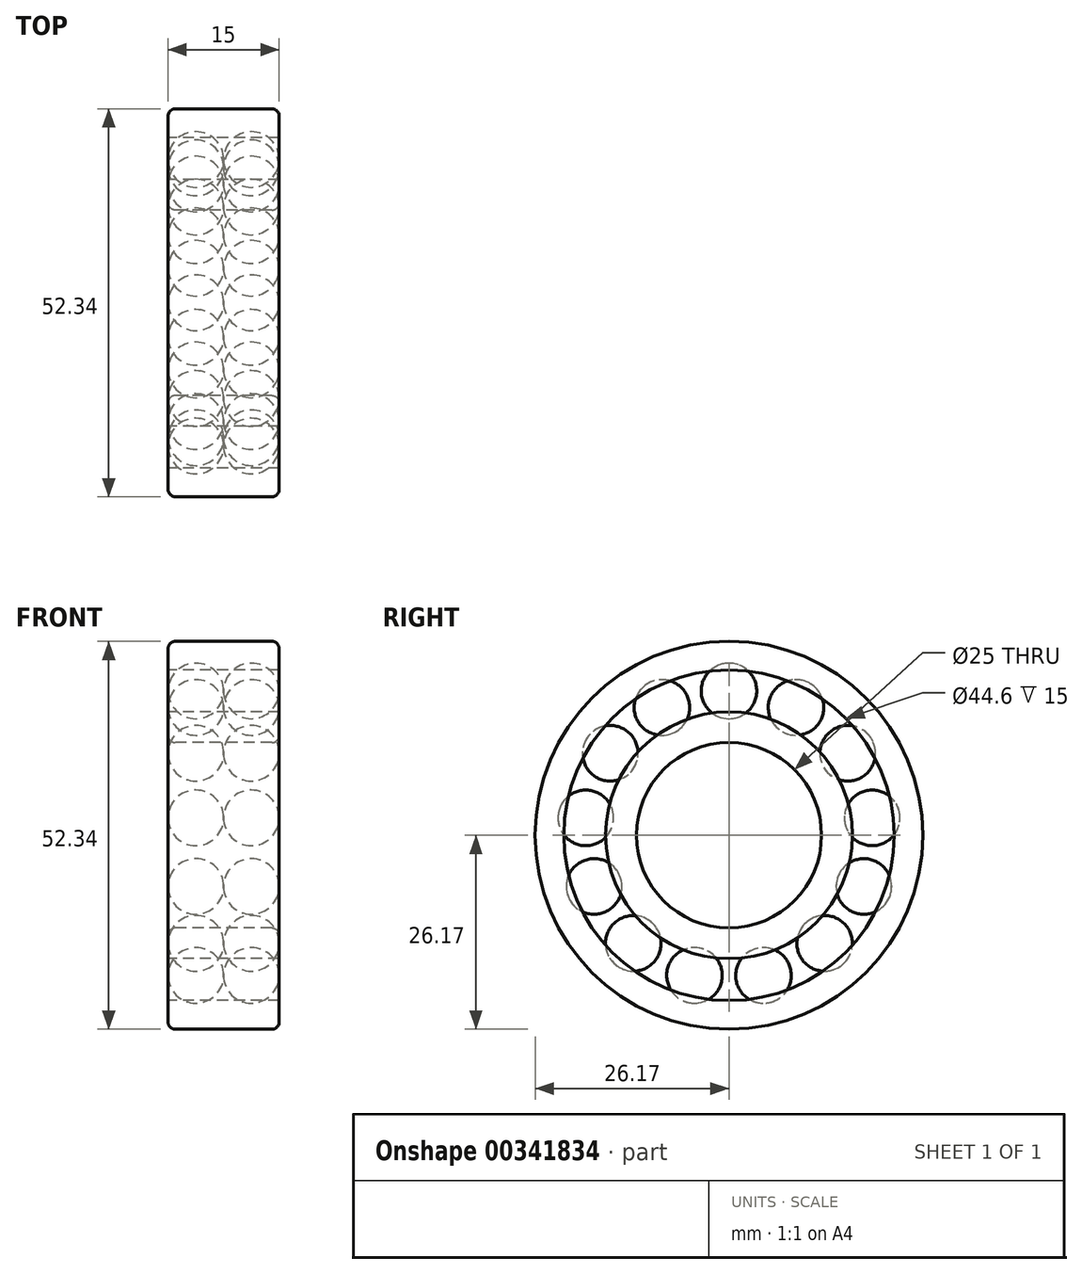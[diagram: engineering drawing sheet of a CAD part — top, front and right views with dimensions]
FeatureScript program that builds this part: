
annotation { "Feature Type Name" : "Feature", "Feature Type Description" : "" }
export const myFeature = defineFeature(function(context is Context, id is Id, definition is map)
    precondition{}
    {
        {
            var Q0;
            Q0=qCreatedBy(makeId("Front.planeOp"),FACE);
            var sketch = newSketch(context, id + "F0", { "sketchPlane" : qUnion([Q0])});
            skLineSegment(sketch, "E0", {"start": v(0, 0) * mm, "end": v(15, 0) * mm});
            skLineSegment(sketch, "E1", {"start": v(14, 12.5) * mm, "end": v(1, 12.5) * mm});
            skLineSegment(sketch, "E2", {"start": v(0, 12.5) * mm, "end": v(0, 16.65) * mm});
            skLineSegment(sketch, "E3", {"start": v(0, 16.65) * mm, "end": v(15, 16.65) * mm});
            skLineSegment(sketch, "E4", {"start": v(15, 16.65) * mm, "end": v(15, 12.5) * mm});
            skLineSegment(sketch, "E5", {"start": v(0, 13.5) * mm, "end": v(0, 16.65) * mm});
            skLineSegment(sketch, "E6", {"start": v(15, 13.5) * mm, "end": v(15, 16.65) * mm});
            skLineSegment(sketch, "E7", {"start": v(15, 22.3) * mm, "end": v(0, 22.3) * mm});
            skLineSegment(sketch, "E8", {"start": v(1, 26.17) * mm, "end": v(14, 26.17) * mm});
            skLineSegment(sketch, "E9", {"start": v(15, 25.17) * mm, "end": v(15, 22.3) * mm});
            skLineSegment(sketch, "E10.trimOffspring", {"start": v(0, 22.3) * mm, "end": v(0, 25.17) * mm});
            skPoint(sketch, "E11.visualSharp", {"position": v(0, 26.17) * mm});
            skArc(sketch, "E11.filletArc", {"start": v(1, 26.17) * mm, "mid": v(0.3, 25.88) * mm, "end": v(0, 25.17) * mm});
            skPoint(sketch, "E12.visualSharp", {"position": v(15, 26.17) * mm});
            skArc(sketch, "E12.filletArc", {"start": v(15, 25.17) * mm, "mid": v(14.7, 25.88) * mm, "end": v(14, 26.17) * mm});
            skPoint(sketch, "E13.visualSharp", {"position": v(15, 12.5) * mm});
            skArc(sketch, "E13.filletArc", {"start": v(14, 12.5) * mm, "mid": v(14.7, 12.8) * mm, "end": v(15, 13.5) * mm});
            skPoint(sketch, "E14.visualSharp", {"position": v(0, 12.5) * mm});
            skArc(sketch, "E14.filletArc", {"start": v(0, 13.5) * mm, "mid": v(0.3, 12.8) * mm, "end": v(1, 12.5) * mm});
            skLineSegment(sketch, "E15", {"start": v(0, 22.3) * mm, "end": v(0, 16.65) * mm});
            skLineSegment(sketch, "E16", {"start": v(0, 19.47) * mm, "end": v(3.75, 19.47) * mm});
            skLineSegment(sketch, "E17", {"start": v(3.75, 19.47) * mm, "end": v(11.25, 19.47) * mm});
            skCircle(sketch, "E18", {"center": v(3.75, 19.47) * mm, "radius": 3.75 * mm});
            skCircle(sketch, "E19", {"center": v(11.25, 19.47) * mm, "radius": 3.75 * mm});
            skLineSegment(sketch, "E20", {"start": v(11.25, 19.47) * mm, "end": v(15, 19.47) * mm});
            skSolve(sketch);
        }
        {
            var Q0;
            Q0=makeQuery(id+"F0.imprint","IMPRINT",FACE,{"disambiguationData":[TD([[makeQuery(id+"F0.imprint","IMPRINT",EDGE,{"derivedFrom":sQuery(id+"F0.wireOp",EDGE,"E8")}),-1.0]])]});
            var Q1;
            {var subQ0=sQuery(id+"F0.wireOp",EDGE,"E18");var subQ1=sQuery(id+"F0.wireOp",EDGE,"E7");var subQ2=makeQuery(id+"F0.imprint","INTERSECT",VERTEX,{"disambiguationData":[OD(0.0)],"derivedFrom":[subQ1,subQ0]});Q1=makeQuery(id+"F0.imprint","IMPRINT",FACE,{"disambiguationData":[TD([[makeQuery(id+"F0.imprint","IMPRINT",EDGE,{"disambiguationData":[TD([[subQ2,-1.0]])],"derivedFrom":subQ1}),-1.0]])]});}
            var Q2;
            {var subQ0=sQuery(id+"F0.wireOp",EDGE,"E19");var subQ1=sQuery(id+"F0.wireOp",EDGE,"E7");var subQ2=makeQuery(id+"F0.imprint","INTERSECT",VERTEX,{"disambiguationData":[OD(0.0)],"derivedFrom":[subQ1,subQ0]});Q2=makeQuery(id+"F0.imprint","IMPRINT",FACE,{"disambiguationData":[TD([[makeQuery(id+"F0.imprint","IMPRINT",EDGE,{"disambiguationData":[TD([[subQ2,-1.0]])],"derivedFrom":subQ1}),-1.0]])]});}
            var Q3;
            {var subQ0=sQuery(id+"F0.wireOp",EDGE,"E19");var subQ1=sQuery(id+"F0.wireOp",EDGE,"E3");var subQ2=makeQuery(id+"F0.imprint","INTERSECT",VERTEX,{"disambiguationData":[OD(0.0)],"derivedFrom":[subQ1,subQ0]});Q3=makeQuery(id+"F0.imprint","IMPRINT",FACE,{"disambiguationData":[TD([[makeQuery(id+"F0.imprint","IMPRINT",EDGE,{"disambiguationData":[TD([[subQ2,1.0]])],"derivedFrom":subQ1}),-1.0]])]});}
            var Q4;
            {var subQ0=sQuery(id+"F0.wireOp",EDGE,"E18");var subQ1=sQuery(id+"F0.wireOp",EDGE,"E3");var subQ2=makeQuery(id+"F0.imprint","INTERSECT",VERTEX,{"disambiguationData":[OD(0.0)],"derivedFrom":[subQ1,subQ0]});Q4=makeQuery(id+"F0.imprint","IMPRINT",FACE,{"disambiguationData":[TD([[makeQuery(id+"F0.imprint","IMPRINT",EDGE,{"disambiguationData":[TD([[subQ2,-1.0]])],"derivedFrom":subQ1}),-1.0]])]});}
            var Q5;
            Q5=makeQuery(id+"F0.imprint","IMPRINT",FACE,{"disambiguationData":[TD([[makeQuery(id+"F0.imprint","IMPRINT",EDGE,{"derivedFrom":sQuery(id+"F0.wireOp",EDGE,"E1")}),-1.0]])]});
            var Q6;
            Q6=sQuery(id+"F0.wireOp",EDGE,"E0");
            revolve(context, id + "F1", {"entities" : qUnion([Q0, Q1, Q2, Q3, Q4, Q5]), "axis" : qUnion([Q6]), "revolveType" : RevolveType.FULL});
        }
        {
            var Q0;
            {var subQ0=sQuery(id+"F0.wireOp",EDGE,"E18");var subQ1=sQuery(id+"F0.wireOp",EDGE,"E7");var subQ2=makeQuery(id+"F0.imprint","INTERSECT",VERTEX,{"disambiguationData":[OD(0.0)],"derivedFrom":[subQ1,subQ0]});Q0=makeQuery(id+"F0.imprint","IMPRINT",FACE,{"disambiguationData":[TD([[makeQuery(id+"F0.imprint","IMPRINT",EDGE,{"disambiguationData":[TD([[subQ2,-1.0]])],"derivedFrom":subQ1}),-1.0]])]});}
            var Q1;
            {var subQ5=sQuery(id+"F0.wireOp",EDGE,"E16");Q1=makeQuery(id+"F0.imprint","IMPRINT",FACE,{"disambiguationData":[TD([[makeQuery(id+"F0.imprint","IMPRINT",EDGE,{"derivedFrom":subQ5}),1.0]])]});}
            var Q2;
            {var subQ5=sQuery(id+"F0.wireOp",EDGE,"E20");Q2=makeQuery(id+"F0.imprint","IMPRINT",FACE,{"disambiguationData":[TD([[makeQuery(id+"F0.imprint","IMPRINT",EDGE,{"derivedFrom":subQ5}),1.0]])]});}
            var Q3;
            {var subQ0=sQuery(id+"F0.wireOp",EDGE,"E19");var subQ1=sQuery(id+"F0.wireOp",EDGE,"E7");var subQ2=makeQuery(id+"F0.imprint","INTERSECT",VERTEX,{"disambiguationData":[OD(0.0)],"derivedFrom":[subQ1,subQ0]});Q3=makeQuery(id+"F0.imprint","IMPRINT",FACE,{"disambiguationData":[TD([[makeQuery(id+"F0.imprint","IMPRINT",EDGE,{"disambiguationData":[TD([[subQ2,-1.0]])],"derivedFrom":subQ1}),-1.0]])]});}
            var Q4;
            Q4=sQuery(id+"F0.wireOp",EDGE,"E17");
            revolve(context, id + "F2", {"entities" : qUnion([Q0, Q1, Q2, Q3]), "axis" : qUnion([Q4]), "revolveType" : RevolveType.FULL});
        }
        {
            var Q0;
            Q0=makeQuery(id+"F2.opRevolve","SWEPT_BODY",BODY,{"disambiguationData":[OSD([sQuery(id+"F0.wireOp",EDGE,"E17"),sQuery(id+"F0.wireOp",EDGE,"E19"),sQuery(id+"F0.wireOp",EDGE,"E20")])]});
            var Q1;
            Q1=makeQuery(id+"F2.opRevolve","SWEPT_BODY",BODY,{"disambiguationData":[OSD([sQuery(id+"F0.wireOp",EDGE,"E16"),sQuery(id+"F0.wireOp",EDGE,"E17"),sQuery(id+"F0.wireOp",EDGE,"E18")])]});
            var Q2;
            Q2=sQuery(id+"F0.wireOp",EDGE,"E0");
            circularPattern(context, id + "F3", {"entities" : qUnion([Q0, Q1]), "axis" : qUnion([Q2]), "angle" : 360 * degree, "instanceCount" : 13, "equalSpace" : true});
        }
    });
